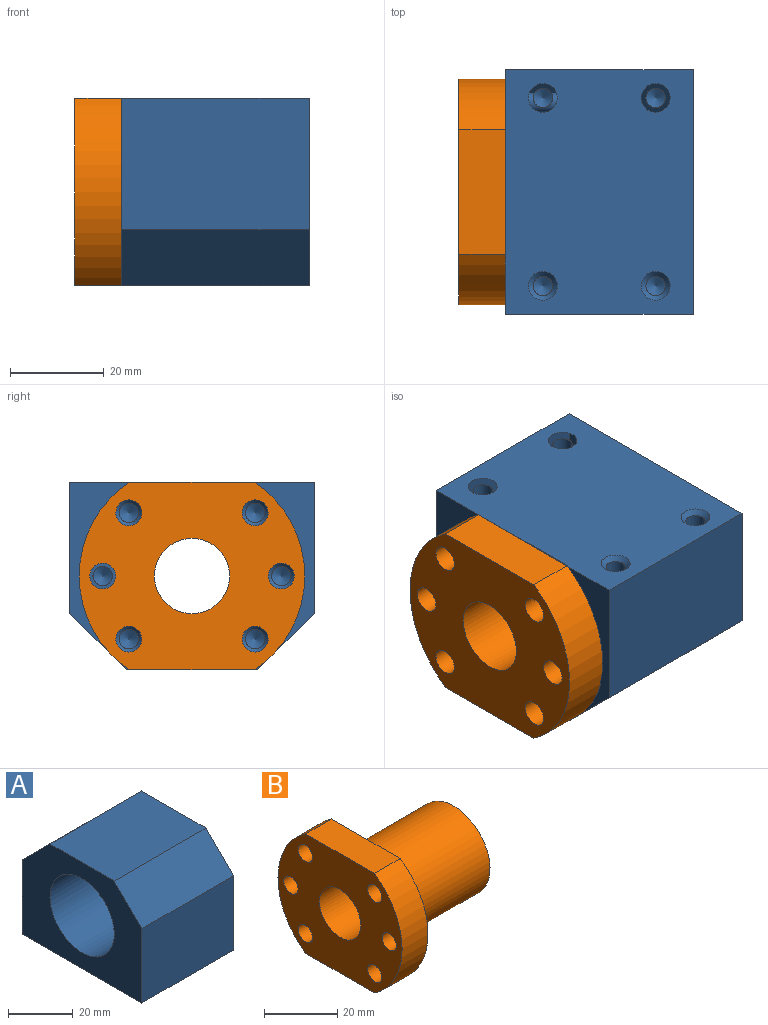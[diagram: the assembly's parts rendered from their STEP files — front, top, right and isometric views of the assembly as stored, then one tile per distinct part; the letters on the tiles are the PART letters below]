
ASSEMBLY  parts=2 mates=1
PART A: 39 faces, bbox 40x52x40 mm
  f0: cone r=0mm half-angle=60deg, axis (1,0,0), area 15.5mm2, adj f6
  f1: cone r=0mm half-angle=60deg, axis (1,0,0), area 15.5mm2, adj f7
  f2: cone r=0mm half-angle=60deg, axis (1,0,0), area 15.5mm2, adj f8
  f3: cone r=0mm half-angle=60deg, axis (1,0,0), area 15.5mm2, adj f9
  f4: cone r=0mm half-angle=60deg, axis (1,0,0), area 15.5mm2, adj f10
  f5: cone r=0mm half-angle=60deg, axis (1,0,0), area 15.5mm2, adj f11
  f6: cylinder r=2.07mm len=11mm, axis (-1,0,0), area 142.9mm2, adj f0,f15
  f7: cylinder r=2.07mm len=11mm, axis (-1,0,0), area 142.9mm2, adj f1,f16
  f8: cylinder r=2.07mm len=11mm, axis (-1,0,0), area 142.9mm2, adj f2,f17
  f9: cylinder r=2.07mm len=11mm, axis (-1,0,0), area 142.9mm2, adj f3,f18
  f10: cylinder r=2.07mm len=11mm, axis (-1,0,0), area 142.9mm2, adj f4,f19
  f11: cylinder r=2.07mm len=11mm, axis (-1,0,0), area 142.9mm2, adj f5,f20
  f12: cone r=0mm half-angle=60deg, axis (0,0,-1), area 15.5mm2, adj f25
  f13: cone r=0mm half-angle=60deg, axis (0,0,-1), area 15.5mm2, adj f26
  f14: cone r=0mm half-angle=60deg, axis (0,0,-1), area 15.5mm2, adj f27
  f15: cone r=2.07mm half-angle=45deg, axis (1,0,0), area 22.8mm2, adj f6,f28
  f16: cone r=2.07mm half-angle=45deg, axis (1,0,0), area 22.8mm2, adj f7,f28
  f17: cone r=2.07mm half-angle=45deg, axis (1,0,0), area 22.8mm2, adj f8,f28
  f18: cone r=2.07mm half-angle=45deg, axis (1,0,0), area 22.8mm2, adj f9,f28
  f19: cone r=2.07mm half-angle=45deg, axis (1,0,0), area 22.8mm2, adj f10,f28
  f20: cone r=2.07mm half-angle=45deg, axis (1,0,0), area 22.8mm2, adj f11,f28
  f21: plane 40x12mm, normal (0,0.71,0.71), area 678.8mm2, adj f22,f28,f29,f30
  f22: plane 40x28mm, normal (0,0,1), area 1120mm2, adj f21,f24,f28,f30
  f23: cylinder r=14mm len=40mm, axis (-1,0,0), area 3518.6mm2, adj f28,f30
  f24: plane 40x12mm, normal (0,-0.71,0.71), area 678.8mm2, adj f22,f28,f30,f31
  f25: cylinder r=2.07mm len=11mm, axis (0,0,1), area 142.9mm2, adj f12,f32
  f26: cylinder r=2.07mm len=11mm, axis (0,0,1), area 142.9mm2, adj f13,f33
  f27: cylinder r=2.07mm len=11mm, axis (0,0,1), area 142.9mm2, adj f14,f34
  f28: plane 52x40mm, normal (1,0,0), area 1142.9mm2, adj f15,f16,f17,f18,f19,f20,f21,f22
  f29: plane 40x28mm, normal (0,1,0), area 1120mm2, adj f21,f28,f30,f35
  f30: plane 52x40mm, normal (-1,0,0), area 1320.2mm2, adj f21,f22,f23,f24,f29,f31,f35
  f31: plane 40x28mm, normal (0,-1,0), area 1120mm2, adj f24,f28,f30,f35
  f32: cone r=2.07mm half-angle=45deg, axis (0,0,-1), area 22.8mm2, adj f25,f35
  f33: cone r=2.07mm half-angle=45deg, axis (0,0,-1), area 22.8mm2, adj f26,f35
  f34: cone r=2.07mm half-angle=45deg, axis (0,0,-1), area 22.8mm2, adj f27,f35
  f35: plane 52x40mm, normal (0,0,-1), area 1961.8mm2, adj f28,f29,f30,f31,f32,f33,f34,f36
  f36: cone r=2.07mm half-angle=45deg, axis (0,0,-1), area 22.8mm2, adj f35,f37
  f37: cylinder r=2.07mm len=11mm, axis (0,0,1), area 142.9mm2, adj f36,f38
  f38: cone r=0mm half-angle=60deg, axis (0,0,-1), area 15.5mm2, adj f37
PART B: 15 faces, bbox 44x48x40 mm
  f0: cylinder r=2.75mm len=10mm, axis (1,0,0), area 172.8mm2, adj f1,f2
  f1: plane 48x40mm, normal (1,0,0), area 907.2mm2, adj f0,f3,f4,f5,f6,f7,f8,f9
  f2: plane 48x40mm, normal (-1,0,0), area 1321.9mm2, adj f0,f3,f4,f5,f7,f8,f9,f10
  f3: plane 26.53x10mm, normal (0,0,1), area 265.3mm2, adj f1,f2,f7,f8
  f4: cylinder r=2.75mm len=10mm, axis (1,0,0), area 172.8mm2, adj f1,f2
  f5: cylinder r=2.75mm len=10mm, axis (1,0,0), area 172.8mm2, adj f1,f2
  f6: cylinder r=14mm len=34mm, axis (-1,0,0), area 2990.8mm2, adj f1,f14
  f7: cylinder r=24mm len=40mm, axis (-1,0,0), area 472.9mm2, adj f1,f2,f3,f10
  f8: cylinder r=24mm len=40mm, axis (-1,0,0), area 472.9mm2, adj f1,f2,f3,f10
  f9: cylinder r=2.75mm len=10mm, axis (1,0,0), area 172.8mm2, adj f1,f2
  f10: plane 26.53x10mm, normal (0,0,-1), area 265.3mm2, adj f1,f2,f7,f8
  f11: cylinder r=2.75mm len=10mm, axis (1,0,0), area 172.8mm2, adj f1,f2
  f12: cylinder r=2.75mm len=10mm, axis (1,0,0), area 172.8mm2, adj f1,f2
  f13: cylinder r=8mm len=44mm, axis (1,0,0), area 2211.7mm2, adj f2,f14
  f14: plane 28x28mm, normal (1,0,0), area 414.7mm2, adj f6,f13
PLACE A rot(axis=(0,1,0),180deg) t=(23.5,-40.25,28.75)mm
PLACE B t=(-6.4,-40.25,8.75)mm
MATE slider A.f3 <-> B.f9  axis (1,0,0) through (10,-59.25,8.75)mm
